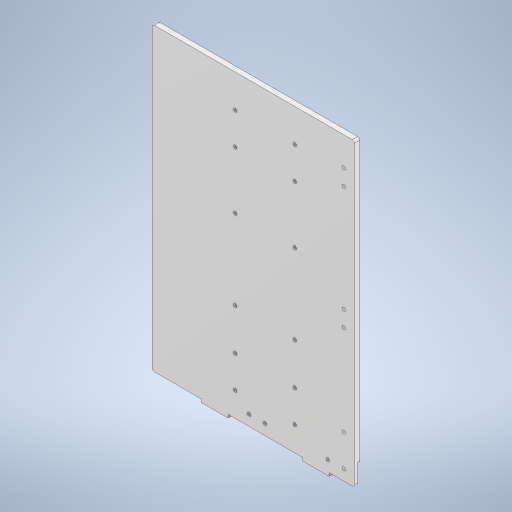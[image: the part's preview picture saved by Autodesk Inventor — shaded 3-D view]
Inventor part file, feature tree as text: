
AUTODESK INVENTOR PART (.ipt)
format: ipt  version: 2024.3 (Build 283343000, 343)  size: 844,800 bytes
history: native  units: mm
features: sketch x12, extrude x9, projected_geometry x6, fillet x4, hole x3
ambient origin geometry x8: Origin, YZ Plane, XZ Plane, XY Plane, X Axis, Y Axis, Z Axis, Center Point
bodies: Body1 (feature_tree)
feature tree (34):
  extrude  "押し出し20"  Depth=190.0mm
  hole  "穴2"  [1 undecoded]
  hole  "穴3"  [1 undecoded]
  extrude  "押し出し21"  Depth=56.0mm
  extrude  "押し出し22"  Depth=30.0mm
  fillet  "フィレット2"  Radius=30.0mm
  extrude  "押し出し23"  Depth=56.0mm
  extrude  "押し出し24"  Depth=56.0mm
  extrude  "押し出し25"  Depth=56.0mm
  fillet  "フィレット3"  Radius=30.0mm
  fillet  "フィレット4"  Radius=30.0mm
  hole  "穴4"  [1 undecoded]
  extrude  "押し出し26"  Depth=75.0mm
  extrude  "押し出し27"  Depth=56.0mm
  extrude  "押し出し28"  Depth=56.0mm
  fillet  "フィレット5"  Radius=26.0mm
  sketch  "スケッチ22"
  sketch  "スケッチ23"
  sketch  "スケッチ24"
  sketch  "スケッチ25"
  sketch  "スケッチ26"
  sketch  "スケッチ27"
  sketch  "スケッチ28"
  projected_geometry  "投影ループ2"
  sketch  "スケッチ29"
  projected_geometry  "投影ループ3"
  sketch  "スケッチ31"
  sketch  "スケッチ32"
  projected_geometry  "投影ループ4"
  projected_geometry  "投影ループ5"
  projected_geometry  "投影ループ6"
  sketch  "スケッチ34"
  sketch  "スケッチ36"
  projected_geometry  "投影ループ8"
note: 3 required parameter values undecoded (feature->parameter linkage not recoverable at this tier; creation-order binding heuristic only, values carry confidence <= 0.55)
